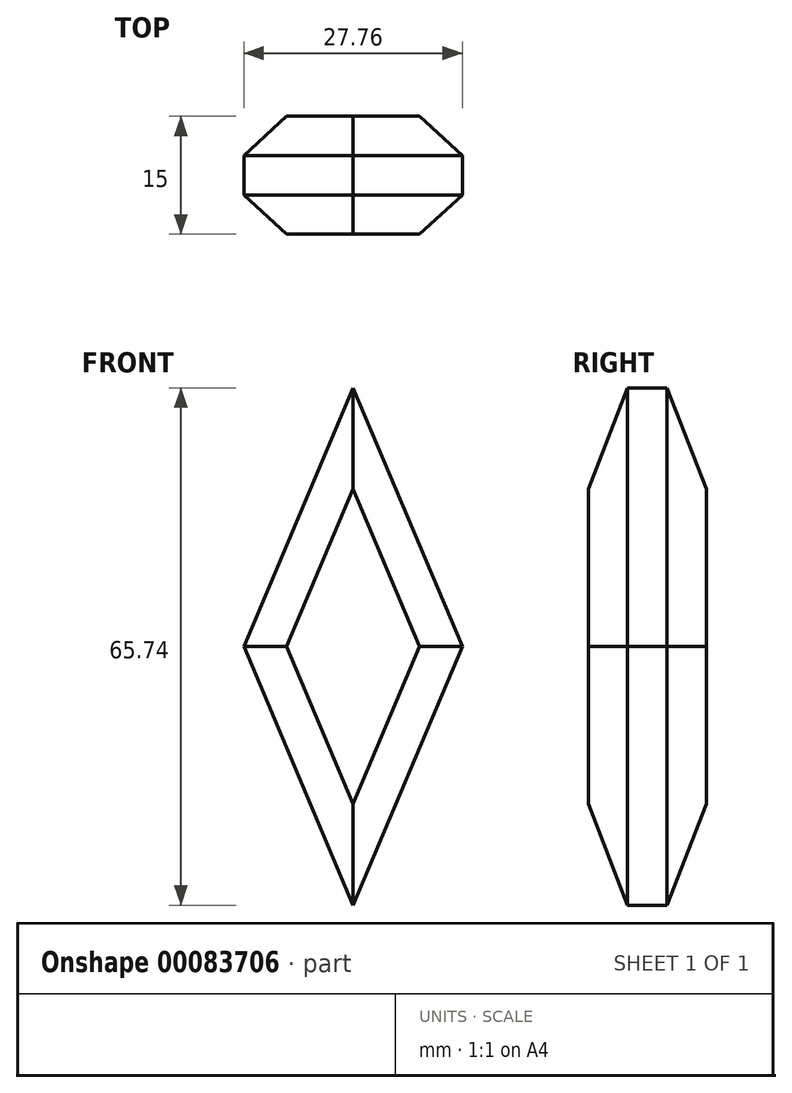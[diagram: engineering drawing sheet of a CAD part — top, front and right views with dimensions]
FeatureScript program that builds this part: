
annotation { "Feature Type Name" : "Feature", "Feature Type Description" : "" }
export const myFeature = defineFeature(function(context is Context, id is Id, definition is map)
    precondition{}
    {
        {
            var Q0;
            Q0=qCreatedBy(makeId("Front.planeOp"),FACE);
            var sketch = newSketch(context, id + "F0", { "sketchPlane" : qUnion([Q0])});
            skLineSegment(sketch, "E0", {"start": v(0, 32.87) * mm, "end": v(-13.88, 0) * mm});
            skLineSegment(sketch, "E1", {"start": v(-13.88, 0) * mm, "end": v(0, -32.87) * mm});
            skLineSegment(sketch, "E2", {"start": v(0, -32.87) * mm, "end": v(13.88, 0) * mm});
            skLineSegment(sketch, "E3", {"start": v(13.88, 0) * mm, "end": v(0, 32.87) * mm});
            skSolve(sketch);
        }
        {
            var Q0;
            Q0 = qSketchRegion(id + "F0", true);
            extrude(context, id + "F1", {"entities" : qUnion([Q0]), "depth" : 15 * mm});
        }
        {
            var Q0;
            {var subQ0=sQuery(id+"F0.wireOp",EDGE,"E0");Q0=makeQuery(id+"F3.opChamfer","BLEND_EDGE",EDGE,{"blendedFrom":[makeQuery(id+"F1.opExtrude","CAP_EDGE",EDGE,{"disambiguationData":[OSD([subQ0])],"isStart":false}),makeQuery(id+"F1.opExtrude","CAP_FACE",FACE,{"disambiguationData":[OSD([subQ0,sQuery(id+"F0.wireOp",EDGE,"E1"),sQuery(id+"F0.wireOp",EDGE,"E2"),sQuery(id+"F0.wireOp",EDGE,"E3")])],"isStart":false})],"blendedInto":[makeQuery(id+"F1.opExtrude","CAP_FACE",FACE,{"disambiguationData":[OSD([subQ0,sQuery(id+"F0.wireOp",EDGE,"E1"),sQuery(id+"F0.wireOp",EDGE,"E2"),sQuery(id+"F0.wireOp",EDGE,"E3")])],"isStart":false})]});}
            var Q1;
            {var subQ0=sQuery(id+"F0.wireOp",EDGE,"E3");Q1=makeQuery(id+"F3.opChamfer","BLEND_EDGE",EDGE,{"blendedFrom":[makeQuery(id+"F1.opExtrude","CAP_EDGE",EDGE,{"disambiguationData":[OSD([subQ0])],"isStart":false}),makeQuery(id+"F1.opExtrude","CAP_FACE",FACE,{"disambiguationData":[OSD([sQuery(id+"F0.wireOp",EDGE,"E0"),sQuery(id+"F0.wireOp",EDGE,"E1"),sQuery(id+"F0.wireOp",EDGE,"E2"),subQ0])],"isStart":false})],"blendedInto":[makeQuery(id+"F1.opExtrude","CAP_FACE",FACE,{"disambiguationData":[OSD([sQuery(id+"F0.wireOp",EDGE,"E0"),sQuery(id+"F0.wireOp",EDGE,"E1"),sQuery(id+"F0.wireOp",EDGE,"E2"),subQ0])],"isStart":false})]});}
            var Q2;
            Q2=makeQuery(id+"F1.opExtrude","CAP_FACE",FACE,{"disambiguationData":[OSD([sQuery(id+"F0.wireOp",EDGE,"E0"),sQuery(id+"F0.wireOp",EDGE,"E1"),sQuery(id+"F0.wireOp",EDGE,"E2"),sQuery(id+"F0.wireOp",EDGE,"E3")])],"isStart":false});
            var Q3;
            {var subQ0=sQuery(id+"F0.wireOp",EDGE,"E2");Q3=makeQuery(id+"F3.opChamfer","BLEND_EDGE",EDGE,{"blendedFrom":[makeQuery(id+"F1.opExtrude","CAP_EDGE",EDGE,{"disambiguationData":[OSD([subQ0])],"isStart":false}),makeQuery(id+"F1.opExtrude","CAP_FACE",FACE,{"disambiguationData":[OSD([sQuery(id+"F0.wireOp",EDGE,"E0"),sQuery(id+"F0.wireOp",EDGE,"E1"),subQ0,sQuery(id+"F0.wireOp",EDGE,"E3")])],"isStart":false})],"blendedInto":[makeQuery(id+"F1.opExtrude","CAP_FACE",FACE,{"disambiguationData":[OSD([sQuery(id+"F0.wireOp",EDGE,"E0"),sQuery(id+"F0.wireOp",EDGE,"E1"),subQ0,sQuery(id+"F0.wireOp",EDGE,"E3")])],"isStart":false})]});}
            var Q4;
            {var subQ0=sQuery(id+"F0.wireOp",EDGE,"E1");Q4=makeQuery(id+"F3.opChamfer","BLEND_EDGE",EDGE,{"blendedFrom":[makeQuery(id+"F1.opExtrude","CAP_EDGE",EDGE,{"disambiguationData":[OSD([subQ0])],"isStart":false}),makeQuery(id+"F1.opExtrude","CAP_FACE",FACE,{"disambiguationData":[OSD([sQuery(id+"F0.wireOp",EDGE,"E0"),subQ0,sQuery(id+"F0.wireOp",EDGE,"E2"),sQuery(id+"F0.wireOp",EDGE,"E3")])],"isStart":false})],"blendedInto":[makeQuery(id+"F1.opExtrude","CAP_FACE",FACE,{"disambiguationData":[OSD([sQuery(id+"F0.wireOp",EDGE,"E0"),subQ0,sQuery(id+"F0.wireOp",EDGE,"E2"),sQuery(id+"F0.wireOp",EDGE,"E3")])],"isStart":false})]});}
            var Q5;
            {var subQ0=sQuery(id+"F0.wireOp",EDGE,"E3");Q5=makeQuery(id+"F3.opChamfer","BLEND_EDGE",EDGE,{"blendedFrom":[makeQuery(id+"F1.opExtrude","CAP_EDGE",EDGE,{"disambiguationData":[OSD([subQ0])],"isStart":true}),makeQuery(id+"F1.opExtrude","CAP_FACE",FACE,{"disambiguationData":[OSD([sQuery(id+"F0.wireOp",EDGE,"E0"),sQuery(id+"F0.wireOp",EDGE,"E1"),sQuery(id+"F0.wireOp",EDGE,"E2"),subQ0])],"isStart":true})],"blendedInto":[makeQuery(id+"F1.opExtrude","CAP_FACE",FACE,{"disambiguationData":[OSD([sQuery(id+"F0.wireOp",EDGE,"E0"),sQuery(id+"F0.wireOp",EDGE,"E1"),sQuery(id+"F0.wireOp",EDGE,"E2"),subQ0])],"isStart":true})]});}
            var Q6;
            {var subQ0=sQuery(id+"F0.wireOp",EDGE,"E2");Q6=makeQuery(id+"F3.opChamfer","BLEND_EDGE",EDGE,{"blendedFrom":[makeQuery(id+"F1.opExtrude","CAP_EDGE",EDGE,{"disambiguationData":[OSD([subQ0])],"isStart":true}),makeQuery(id+"F1.opExtrude","CAP_FACE",FACE,{"disambiguationData":[OSD([sQuery(id+"F0.wireOp",EDGE,"E0"),sQuery(id+"F0.wireOp",EDGE,"E1"),subQ0,sQuery(id+"F0.wireOp",EDGE,"E3")])],"isStart":true})],"blendedInto":[makeQuery(id+"F1.opExtrude","CAP_FACE",FACE,{"disambiguationData":[OSD([sQuery(id+"F0.wireOp",EDGE,"E0"),sQuery(id+"F0.wireOp",EDGE,"E1"),subQ0,sQuery(id+"F0.wireOp",EDGE,"E3")])],"isStart":true})]});}
            var Q7;
            {var subQ0=sQuery(id+"F0.wireOp",EDGE,"E1");Q7=makeQuery(id+"F3.opChamfer","BLEND_EDGE",EDGE,{"blendedFrom":[makeQuery(id+"F1.opExtrude","CAP_EDGE",EDGE,{"disambiguationData":[OSD([subQ0])],"isStart":true}),makeQuery(id+"F1.opExtrude","CAP_FACE",FACE,{"disambiguationData":[OSD([sQuery(id+"F0.wireOp",EDGE,"E0"),subQ0,sQuery(id+"F0.wireOp",EDGE,"E2"),sQuery(id+"F0.wireOp",EDGE,"E3")])],"isStart":true})],"blendedInto":[makeQuery(id+"F1.opExtrude","CAP_FACE",FACE,{"disambiguationData":[OSD([sQuery(id+"F0.wireOp",EDGE,"E0"),subQ0,sQuery(id+"F0.wireOp",EDGE,"E2"),sQuery(id+"F0.wireOp",EDGE,"E3")])],"isStart":true})]});}
            var Q8;
            {var subQ0=sQuery(id+"F0.wireOp",EDGE,"E0");Q8=makeQuery(id+"F3.opChamfer","BLEND_EDGE",EDGE,{"blendedFrom":[makeQuery(id+"F1.opExtrude","CAP_EDGE",EDGE,{"disambiguationData":[OSD([subQ0])],"isStart":true}),makeQuery(id+"F1.opExtrude","CAP_FACE",FACE,{"disambiguationData":[OSD([subQ0,sQuery(id+"F0.wireOp",EDGE,"E1"),sQuery(id+"F0.wireOp",EDGE,"E2"),sQuery(id+"F0.wireOp",EDGE,"E3")])],"isStart":true})],"blendedInto":[makeQuery(id+"F1.opExtrude","CAP_FACE",FACE,{"disambiguationData":[OSD([subQ0,sQuery(id+"F0.wireOp",EDGE,"E1"),sQuery(id+"F0.wireOp",EDGE,"E2"),sQuery(id+"F0.wireOp",EDGE,"E3")])],"isStart":true})]});}
            chamfer(context, id + "F2", {"entities" : qUnion([Q0, Q1, Q2, Q3, Q4, Q5, Q6, Q7, Q8]), "width" : 5 * mm, "tangentPropagation" : true});
        }
        {
            var Q0;
            Q0=makeQuery(id+"F1.opExtrude","CAP_EDGE",EDGE,{"disambiguationData":[OSD([sQuery(id+"F0.wireOp",EDGE,"E2")])],"isStart":false});
            var Q1;
            Q1=makeQuery(id+"F1.opExtrude","CAP_EDGE",EDGE,{"disambiguationData":[OSD([sQuery(id+"F0.wireOp",EDGE,"E0")])],"isStart":false});
            var Q2;
            Q2=makeQuery(id+"F1.opExtrude","CAP_EDGE",EDGE,{"disambiguationData":[OSD([sQuery(id+"F0.wireOp",EDGE,"E1")])],"isStart":false});
            var Q3;
            Q3=makeQuery(id+"F1.opExtrude","CAP_EDGE",EDGE,{"disambiguationData":[OSD([sQuery(id+"F0.wireOp",EDGE,"E2")])],"isStart":true});
            var Q4;
            Q4=makeQuery(id+"F1.opExtrude","CAP_EDGE",EDGE,{"disambiguationData":[OSD([sQuery(id+"F0.wireOp",EDGE,"E3")])],"isStart":false});
            var Q5;
            Q5=makeQuery(id+"F1.opExtrude","CAP_EDGE",EDGE,{"disambiguationData":[OSD([sQuery(id+"F0.wireOp",EDGE,"E0")])],"isStart":true});
            var Q6;
            Q6=makeQuery(id+"F1.opExtrude","CAP_EDGE",EDGE,{"disambiguationData":[OSD([sQuery(id+"F0.wireOp",EDGE,"E3")])],"isStart":true});
            var Q7;
            Q7=makeQuery(id+"F1.opExtrude","CAP_EDGE",EDGE,{"disambiguationData":[OSD([sQuery(id+"F0.wireOp",EDGE,"E1")])],"isStart":true});
            chamfer(context, id + "F3", {"entities" : qUnion([Q0, Q1, Q2, Q3, Q4, Q5, Q6, Q7]), "width" : 5 * mm, "tangentPropagation" : true});
        }
    });
